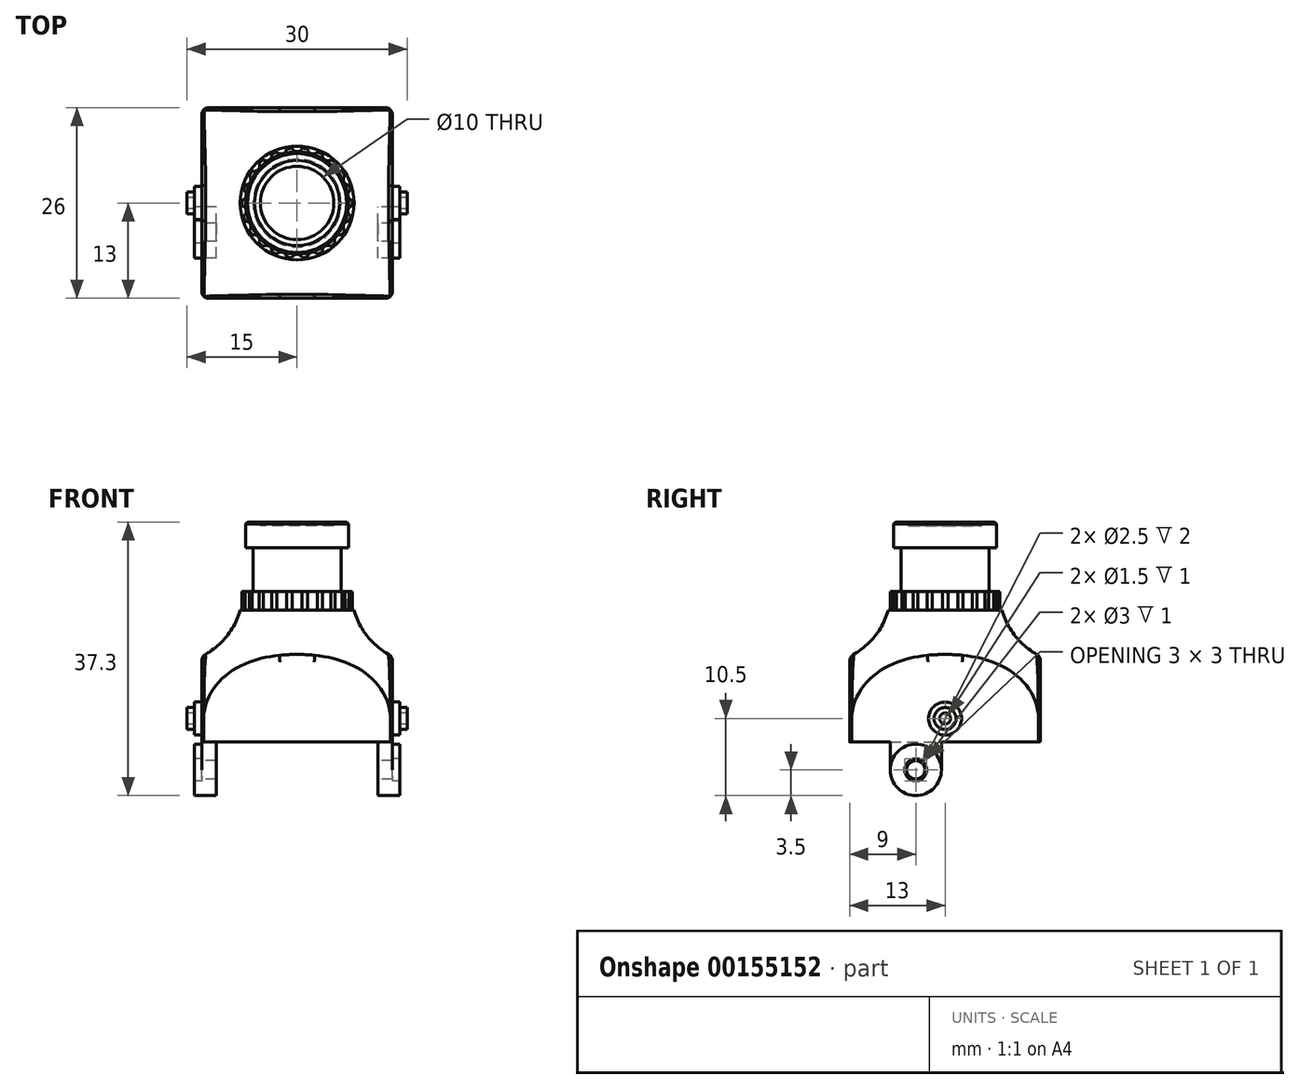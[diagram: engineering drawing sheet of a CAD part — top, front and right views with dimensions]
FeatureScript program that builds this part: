
annotation { "Feature Type Name" : "Feature", "Feature Type Description" : "" }
export const myFeature = defineFeature(function(context is Context, id is Id, definition is map)
    precondition{}
    {
        {
            var Q0;
            Q0=qCreatedBy(makeId("Front.planeOp"),FACE);
            var sketch = newSketch(context, id + "F0", { "sketchPlane" : qUnion([Q0])});
            skLineSegment(sketch, "E0", {"start": v(0, 83.46) * mm, "end": v(0, 0) * mm, "construction": true});
            skLineSegment(sketch, "E1", {"start": v(5, 30) * mm, "end": v(7, 30) * mm});
            skLineSegment(sketch, "E2", {"start": v(7, 30) * mm, "end": v(7, 26.5) * mm});
            skLineSegment(sketch, "E3", {"start": v(7, 26.5) * mm, "end": v(6, 26.5) * mm});
            skLineSegment(sketch, "E4", {"start": v(6, 26.5) * mm, "end": v(6, 20.5) * mm});
            skLineSegment(sketch, "E5", {"start": v(6, 20.5) * mm, "end": v(7.5, 20.5) * mm});
            skLineSegment(sketch, "E6", {"start": v(7.5, 20.5) * mm, "end": v(7.5, 18) * mm});
            skLineSegment(sketch, "E7", {"start": v(7.75, 18) * mm, "end": v(7.5, 18) * mm});
            skLineSegment(sketch, "E8", {"start": v(18, 3) * mm, "end": v(18, 0) * mm});
            skLineSegment(sketch, "E9", {"start": v(18, 0) * mm, "end": v(0, 0) * mm});
            skArc(sketch, "E10", {"start": v(7.75, 18) * mm, "mid": v(9.59, 14.4) * mm, "end": v(12.7, 11.83) * mm});
            skArc(sketch, "E11", {"start": v(18, 3) * mm, "mid": v(16.57, 8.15) * mm, "end": v(12.7, 11.83) * mm});
            skLineSegment(sketch, "E12", {"start": v(5, 30) * mm, "end": v(5, 29.5) * mm});
            skLineSegment(sketch, "E13", {"start": v(0, 29.36) * mm, "end": v(0, 0) * mm});
            skLineSegment(sketch, "E14", {"start": v(0, 29.86) * mm, "end": v(0, 29.36) * mm});
            skArc(sketch, "E15", {"start": v(5, 29.5) * mm, "mid": v(2.5, 29.77) * mm, "end": v(0, 29.86) * mm});
            skSolve(sketch);
        }
        {
            var Q0;
            Q0=makeQuery(id+"F0.imprint","IMPRINT",FACE,{"disambiguationData":[TD([[makeQuery(id+"F0.imprint","IMPRINT",EDGE,{"derivedFrom":sQuery(id+"F0.wireOp",EDGE,"E1")}),-1.0]])]});
            var Q1;
            Q1=sQuery(id+"F0.wireOp",EDGE,"E0");
            revolve(context, id + "F1", {"entities" : qUnion([Q0]), "axis" : qUnion([Q1]), "revolveType" : RevolveType.FULL});
        }
        {
            var Q0;
            Q0=makeQuery(id+"F1.opRevolve","SWEPT_FACE",FACE,{"disambiguationData":[OSD([sQuery(id+"F0.wireOp",EDGE,"E9")])]});
            var sketch = newSketch(context, id + "F2", { "sketchPlane" : qUnion([Q0])});
            skLineSegment(sketch, "E16.bottom", {"start": v(-13, 13) * mm, "end": v(13, 13) * mm});
            skLineSegment(sketch, "E16.top", {"start": v(-13, -13) * mm, "end": v(13, -13) * mm});
            skLineSegment(sketch, "E16.left", {"start": v(-13, 13) * mm, "end": v(-13, -13) * mm});
            skLineSegment(sketch, "E16.right", {"start": v(13, 13) * mm, "end": v(13, -13) * mm});
            skCircle(sketch, "E17", {"center": v(0, 0) * mm, "radius": 20 * mm});
            skSolve(sketch);
        }
        {
            var Q0;
            Q0=qSketchRegion(id+"F2",true);
            extrude(context, id + "F3", {"entities" : qUnion([Q0]), "operationType" : NewBodyOperationType.REMOVE, "oppositeDirection" : true, "depth" : 15 * mm});
        }
        {
            var Q0;
            Q0=makeQuery(id+"F3.boolean.opBoolean","INTERSECT",EDGE,{"disambiguationData":[OD(1.0)],"derivedFrom":[makeQuery(id+"F1.opRevolve","SWEPT_FACE",FACE,{"disambiguationData":[OSD([sQuery(id+"F0.wireOp",EDGE,"E8")])]}),makeQuery(id+"F3.opExtrude","SWEPT_FACE",FACE,{"disambiguationData":[OSD([sQuery(id+"F2.wireOp",EDGE,"E16.left")])]})]});
            var Q1;
            Q1=makeQuery(id+"F3.boolean.opBoolean","INTERSECT",EDGE,{"disambiguationData":[OD(1.0)],"derivedFrom":[makeQuery(id+"F1.opRevolve","SWEPT_FACE",FACE,{"disambiguationData":[OSD([sQuery(id+"F0.wireOp",EDGE,"E11")])]}),makeQuery(id+"F3.opExtrude","SWEPT_FACE",FACE,{"disambiguationData":[OSD([sQuery(id+"F2.wireOp",EDGE,"E16.left")])]})]});
            var Q2;
            Q2=makeQuery(id+"F3.boolean.opBoolean","INTERSECT",EDGE,{"derivedFrom":[makeQuery(id+"F1.opRevolve","SWEPT_FACE",FACE,{"disambiguationData":[OSD([sQuery(id+"F0.wireOp",EDGE,"E10")])]}),makeQuery(id+"F3.opExtrude","SWEPT_FACE",FACE,{"disambiguationData":[OSD([sQuery(id+"F2.wireOp",EDGE,"E16.left")])]})]});
            var Q3;
            Q3=makeQuery(id+"F3.boolean.opBoolean","INTERSECT",EDGE,{"disambiguationData":[OD(0.0)],"derivedFrom":[makeQuery(id+"F1.opRevolve","SWEPT_FACE",FACE,{"disambiguationData":[OSD([sQuery(id+"F0.wireOp",EDGE,"E11")])]}),makeQuery(id+"F3.opExtrude","SWEPT_FACE",FACE,{"disambiguationData":[OSD([sQuery(id+"F2.wireOp",EDGE,"E16.left")])]})]});
            var Q4;
            Q4=makeQuery(id+"F3.boolean.opBoolean","INTERSECT",EDGE,{"disambiguationData":[OD(0.0)],"derivedFrom":[makeQuery(id+"F1.opRevolve","SWEPT_FACE",FACE,{"disambiguationData":[OSD([sQuery(id+"F0.wireOp",EDGE,"E8")])]}),makeQuery(id+"F3.opExtrude","SWEPT_FACE",FACE,{"disambiguationData":[OSD([sQuery(id+"F2.wireOp",EDGE,"E16.left")])]})]});
            var Q5;
            Q5=makeQuery(id+"F3.boolean.opBoolean","INTERSECT",EDGE,{"disambiguationData":[OD(0.0)],"derivedFrom":[makeQuery(id+"F1.opRevolve","SWEPT_FACE",FACE,{"disambiguationData":[OSD([sQuery(id+"F0.wireOp",EDGE,"E8")])]}),makeQuery(id+"F3.opExtrude","SWEPT_FACE",FACE,{"disambiguationData":[OSD([sQuery(id+"F2.wireOp",EDGE,"E16.top")])]})]});
            var Q6;
            Q6=makeQuery(id+"F3.boolean.opBoolean","INTERSECT",EDGE,{"disambiguationData":[OD(1.0)],"derivedFrom":[makeQuery(id+"F1.opRevolve","SWEPT_FACE",FACE,{"disambiguationData":[OSD([sQuery(id+"F0.wireOp",EDGE,"E8")])]}),makeQuery(id+"F3.opExtrude","SWEPT_FACE",FACE,{"disambiguationData":[OSD([sQuery(id+"F2.wireOp",EDGE,"E16.right")])]})]});
            var Q7;
            Q7=makeQuery(id+"F3.boolean.opBoolean","INTERSECT",EDGE,{"disambiguationData":[OD(1.0)],"derivedFrom":[makeQuery(id+"F1.opRevolve","SWEPT_FACE",FACE,{"disambiguationData":[OSD([sQuery(id+"F0.wireOp",EDGE,"E8")])]}),makeQuery(id+"F3.opExtrude","SWEPT_FACE",FACE,{"disambiguationData":[OSD([sQuery(id+"F2.wireOp",EDGE,"E16.bottom")])]})]});
            fillet(context, id + "F4", {"entities" : qUnion([Q0, Q1, Q2, Q3, Q4, Q5, Q6, Q7]), "radius" : 1 * mm, "tangentPropagation" : true, "allowEdgeOverflow" : false});
        }
        {
            var Q0;
            Q0=makeQuery(id+"F1.opRevolve","SWEPT_FACE",FACE,{"disambiguationData":[OSD([sQuery(id+"F0.wireOp",EDGE,"E5")])]});
            var sketch = newSketch(context, id + "F5", { "sketchPlane" : qUnion([Q0])});
            skCircle(sketch, "E18", {"center": v(0, 7.75) * mm, "radius": 0.75 * mm});
            skCircle(sketch, "E19.1.0", {"center": v(-2.18, 7.44) * mm, "radius": 0.75 * mm});
            skCircle(sketch, "E19.2.0", {"center": v(-4.19, 6.52) * mm, "radius": 0.75 * mm});
            skCircle(sketch, "E19.3.0", {"center": v(-5.86, 5.08) * mm, "radius": 0.75 * mm});
            skCircle(sketch, "E19.4.0", {"center": v(-7.05, 3.22) * mm, "radius": 0.75 * mm});
            skCircle(sketch, "E19.5.0", {"center": v(-7.67, 1.1) * mm, "radius": 0.75 * mm});
            skCircle(sketch, "E19.6.0", {"center": v(-7.67, -1.1) * mm, "radius": 0.75 * mm});
            skCircle(sketch, "E19.7.0", {"center": v(-7.05, -3.22) * mm, "radius": 0.75 * mm});
            skCircle(sketch, "E19.8.0", {"center": v(-5.86, -5.08) * mm, "radius": 0.75 * mm});
            skCircle(sketch, "E19.9.0", {"center": v(-4.19, -6.52) * mm, "radius": 0.75 * mm});
            skCircle(sketch, "E19.10.0", {"center": v(-2.18, -7.44) * mm, "radius": 0.75 * mm});
            skCircle(sketch, "E19.11.0", {"center": v(0, -7.75) * mm, "radius": 0.75 * mm});
            skCircle(sketch, "E19.12.0", {"center": v(2.18, -7.44) * mm, "radius": 0.75 * mm});
            skCircle(sketch, "E19.13.0", {"center": v(4.19, -6.52) * mm, "radius": 0.75 * mm});
            skCircle(sketch, "E19.14.0", {"center": v(5.86, -5.08) * mm, "radius": 0.75 * mm});
            skCircle(sketch, "E19.15.0", {"center": v(7.05, -3.22) * mm, "radius": 0.75 * mm});
            skCircle(sketch, "E19.16.0", {"center": v(7.67, -1.1) * mm, "radius": 0.75 * mm});
            skCircle(sketch, "E19.17.0", {"center": v(7.67, 1.1) * mm, "radius": 0.75 * mm});
            skCircle(sketch, "E19.18.0", {"center": v(7.05, 3.22) * mm, "radius": 0.75 * mm});
            skCircle(sketch, "E19.19.0", {"center": v(5.86, 5.08) * mm, "radius": 0.75 * mm});
            skCircle(sketch, "E19.20.0", {"center": v(4.19, 6.52) * mm, "radius": 0.75 * mm});
            skCircle(sketch, "E19.21.0", {"center": v(2.18, 7.44) * mm, "radius": 0.75 * mm});
            skPoint(sketch, "E19.center", {"position": v(0, 0) * mm});
            skCircle(sketch, "E20", {"center": v(0, 0) * mm, "radius": 7.75 * mm, "construction": true});
            skLineSegment(sketch, "E21", {"start": v(0, 7.75) * mm, "end": v(0, 0) * mm, "construction": true});
            skLineSegment(sketch, "E22", {"start": v(0, 0) * mm, "end": v(2.18, 7.44) * mm, "construction": true});
            skSolve(sketch);
        }
        {
            var Q0;
            Q0=qSketchRegion(id+"F5",true);
            extrude(context, id + "F6", {"entities" : qUnion([Q0]), "operationType" : NewBodyOperationType.REMOVE, "oppositeDirection" : true, "depth" : 2.5 * mm});
        }
        {
            var Q0;
            Q0=makeQuery(id+"F1.opRevolve","SWEPT_EDGE",EDGE,{"disambiguationData":[OSD([sQuery(id+"F0.wireOp",EDGE,"E1"),sQuery(id+"F0.wireOp",EDGE,"E2")])]});
            chamfer(context, id + "F7", {"entities" : qUnion([Q0]), "width" : 0.25 * mm, "tangentPropagation" : true});
        }
        {
            var Q0;
            Q0=makeQuery(id+"F1.opRevolve","SWEPT_EDGE",EDGE,{"disambiguationData":[OSD([sQuery(id+"F0.wireOp",EDGE,"E1"),sQuery(id+"F0.wireOp",EDGE,"E12")])]});
            chamfer(context, id + "F8", {"entities" : qUnion([Q0]), "chamferType" : ChamferType.TWO_OFFSETS, "width1" : 0.4 * mm, "oppositeDirection" : false, "width2" : 0.8 * mm, "tangentPropagation" : true});
        }
        {
            var Q0;
            Q0=qCreatedBy(makeId("Right.planeOp"),FACE);
            var sketch = newSketch(context, id + "F9", { "sketchPlane" : qUnion([Q0])});
            skCircle(sketch, "E23", {"center": v(0, 3.2) * mm, "radius": 2.25 * mm});
            skSolve(sketch);
        }
        {
            var Q0;
            Q0=qSketchRegion(id+"F9",true);
            extrude(context, id + "F10", {"entities" : qUnion([Q0]), "operationType" : NewBodyOperationType.ADD, "endBound" : BoundingType.SYMMETRIC, "depth" : 28 * mm});
        }
        {
            var Q0;
            Q0=qCreatedBy(makeId("Right.planeOp"),FACE);
            var sketch = newSketch(context, id + "F11", { "sketchPlane" : qUnion([Q0])});
            skCircle(sketch, "E24", {"center": v(0, 3.2) * mm, "radius": 1.5 * mm});
            skCircle(sketch, "E25", {"center": v(0, 3.2) * mm, "radius": 0.75 * mm});
            skSolve(sketch);
        }
        {
            var Q0;
            Q0=qSketchRegion(id+"F11",true);
            extrude(context, id + "F12", {"entities" : qUnion([Q0]), "operationType" : NewBodyOperationType.ADD, "endBound" : BoundingType.SYMMETRIC, "depth" : 30 * mm});
        }
        {
            var Q0;
            Q0=qCreatedBy(makeId("Right.planeOp"),FACE);
            var sketch = newSketch(context, id + "F13", { "sketchPlane" : qUnion([Q0])});
            skLineSegment(sketch, "E26.bottom", {"start": v(-7.5, 0) * mm, "end": v(-0.5, 0) * mm});
            skLineSegment(sketch, "E26.left", {"start": v(-7.5, 0) * mm, "end": v(-7.5, -3.8) * mm});
            skLineSegment(sketch, "E26.right", {"start": v(-0.5, 0) * mm, "end": v(-0.5, -3.8) * mm});
            skArc(sketch, "E27", {"start": v(-7.5, -3.8) * mm, "mid": v(-4, -7.3) * mm, "end": v(-0.5, -3.8) * mm});
            skCircle(sketch, "E28", {"center": v(-4, -3.8) * mm, "radius": 1.25 * mm});
            skLineSegment(sketch, "E29", {"start": v(-7.5, -3.8) * mm, "end": v(-0.5, -3.8) * mm, "construction": true});
            skSolve(sketch);
        }
        {
            var Q0;
            Q0 = qSketchRegion(id + "F13", true);
            extrude(context, id + "F14", {"entities" : qUnion([Q0]), "operationType" : NewBodyOperationType.ADD, "endBound" : BoundingType.SYMMETRIC, "depth" : 26 * mm});
        }
        {
            var Q0;
            Q0=qCreatedBy(makeId("Right.planeOp"),FACE);
            var sketch = newSketch(context, id + "F15", { "sketchPlane" : qUnion([Q0])});
            skCircle(sketch, "E30", {"center": v(-4, -3.8) * mm, "radius": 3.5 * mm});
            skCircle(sketch, "E31", {"center": v(-4, -3.8) * mm, "radius": 1.5 * mm});
            skSolve(sketch);
        }
        {
            var Q0;
            Q0 = qSketchRegion(id + "F15", true);
            extrude(context, id + "F16", {"entities" : qUnion([Q0]), "operationType" : NewBodyOperationType.ADD, "endBound" : BoundingType.SYMMETRIC, "depth" : 28 * mm});
        }
        {
            var Q0;
            Q0=qCreatedBy(makeId("Top.planeOp"),FACE);
            var sketch = newSketch(context, id + "F17", { "sketchPlane" : qUnion([Q0])});
            skLineSegment(sketch, "E32.bottom", {"start": v(-11, -13) * mm, "end": v(11, -13) * mm});
            skLineSegment(sketch, "E32.top", {"start": v(-11, 13) * mm, "end": v(11, 13) * mm});
            skLineSegment(sketch, "E32.left", {"start": v(-11, -13) * mm, "end": v(-11, 13) * mm});
            skLineSegment(sketch, "E32.right", {"start": v(11, -13) * mm, "end": v(11, 13) * mm});
            skSolve(sketch);
        }
        {
            var Q0;
            Q0 = qSketchRegion(id + "F17", true);
            extrude(context, id + "F18", {"entities" : qUnion([Q0]), "operationType" : NewBodyOperationType.REMOVE, "oppositeDirection" : true, "depth" : 25 * mm});
        }
    });
